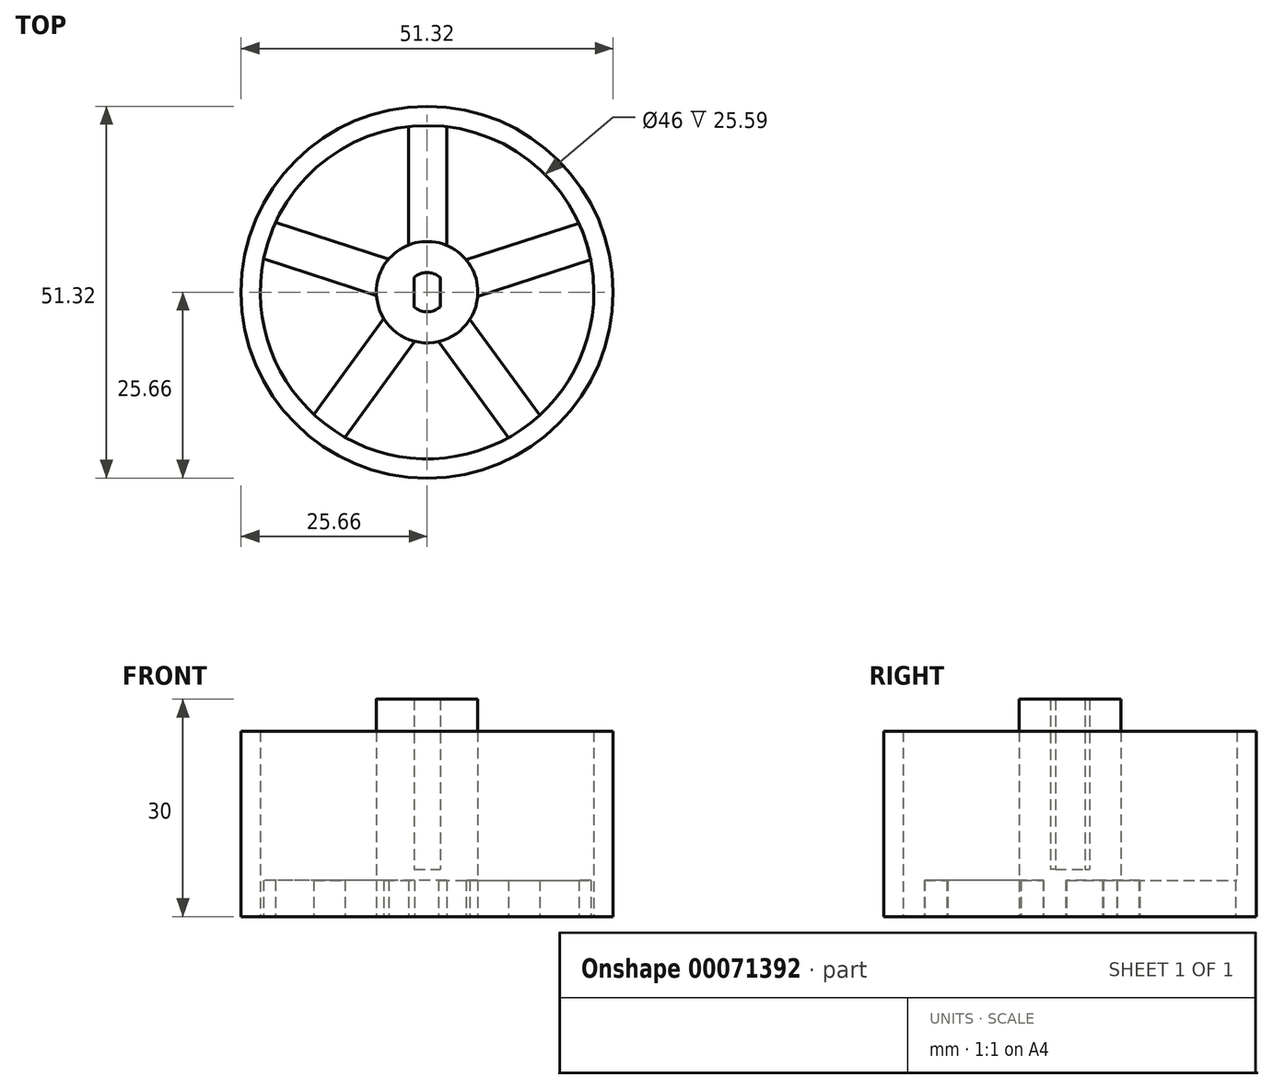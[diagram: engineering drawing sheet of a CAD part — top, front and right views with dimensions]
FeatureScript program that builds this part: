
annotation { "Feature Type Name" : "Feature", "Feature Type Description" : "" }
export const myFeature = defineFeature(function(context is Context, id is Id, definition is map)
    precondition{}
    {
        {
            var Q0;
            Q0=qCreatedBy(makeId("Top.planeOp"),FACE);
            var sketch = newSketch(context, id + "F0", { "sketchPlane" : qUnion([Q0])});
            skCircle(sketch, "E0", {"center": v(0, 0) * mm, "radius": 7 * mm});
            skCircle(sketch, "E1", {"center": v(0, 0) * mm, "radius": 23 * mm});
            skCircle(sketch, "E2", {"center": v(0, 0) * mm, "radius": 25.66 * mm});
            skLineSegment(sketch, "E3", {"start": v(-2.59, 6.5) * mm, "end": v(-2.59, 22.85) * mm});
            skLineSegment(sketch, "E4", {"start": v(2.71, 6.45) * mm, "end": v(2.71, 22.84) * mm});
            skLineSegment(sketch, "E5", {"start": v(-42.68, 0) * mm, "end": v(36.45, 0) * mm, "construction": true});
            skLineSegment(sketch, "E6", {"start": v(0, -31.73) * mm, "end": v(0, 31.16) * mm, "construction": true});
            skLineSegment(sketch, "E7.1.0", {"start": v(-6.99, -0.45) * mm, "end": v(-22.53, 4.6) * mm});
            skLineSegment(sketch, "E7.1.1", {"start": v(-5.3, 4.57) * mm, "end": v(-20.88, 9.64) * mm});
            skLineSegment(sketch, "E7.2.0", {"start": v(-1.73, -6.78) * mm, "end": v(-11.34, -20) * mm});
            skLineSegment(sketch, "E7.2.1", {"start": v(-5.99, -3.63) * mm, "end": v(-15.62, -16.88) * mm});
            skLineSegment(sketch, "E7.3.0", {"start": v(5.92, -3.74) * mm, "end": v(15.52, -16.97) * mm});
            skLineSegment(sketch, "E7.3.1", {"start": v(1.6, -6.82) * mm, "end": v(11.23, -20.07) * mm});
            skLineSegment(sketch, "E7.4.0", {"start": v(5.39, 4.47) * mm, "end": v(20.94, 9.52) * mm});
            skLineSegment(sketch, "E7.4.1", {"start": v(6.98, -0.59) * mm, "end": v(22.56, 4.48) * mm});
            skArc(sketch, "E8", {"start": v(-1.8, -2.03) * mm, "mid": v(0, -2.71) * mm, "end": v(1.8, -2.03) * mm});
            skLineSegment(sketch, "E9.left", {"start": v(1.8, -2.03) * mm, "end": v(1.8, 2.03) * mm});
            skLineSegment(sketch, "E9.right", {"start": v(-1.8, -2.03) * mm, "end": v(-1.8, 2.03) * mm});
            skArc(sketch, "E10.trimOffspring", {"start": v(1.8, 2.03) * mm, "mid": v(0, 2.72) * mm, "end": v(-1.8, 2.03) * mm});
            skSolve(sketch);
        }
        {
            var Q0;
            Q0=makeQuery(id+"F0.imprint","IMPRINT",FACE,{"disambiguationData":[TD([[makeQuery(id+"F0.imprint","IMPRINT",EDGE,{"derivedFrom":sQuery(id+"F0.wireOp",EDGE,"E9.bottom")}),-1.0]])]});
            var Q1;
            Q1=makeQuery(id+"F0.imprint","IMPRINT",FACE,{"disambiguationData":[TD([[makeQuery(id+"F0.imprint","IMPRINT",EDGE,{"derivedFrom":sQuery(id+"F0.wireOp",EDGE,"E8")}),1.0]])]});
            var Q2;
            Q2=makeQuery(id+"F0.imprint","IMPRINT",FACE,{"disambiguationData":[TD([[makeQuery(id+"F0.imprint","IMPRINT",EDGE,{"derivedFrom":sQuery(id+"F0.wireOp",EDGE,"E9.top")}),-1.0]])]});
            extrude(context, id + "F1", {"entities" : qUnion([Q0, Q1, Q2]), "depth" : 6.5 * mm});
        }
        {
            var Q0;
            Q0=makeQuery(id+"F0.imprint","IMPRINT",FACE,{"disambiguationData":[TD([[makeQuery(id+"F0.imprint","IMPRINT",EDGE,{"derivedFrom":sQuery(id+"F0.wireOp",EDGE,"E1")}),-1.0]])]});
            extrude(context, id + "F2", {"entities" : qUnion([Q0]), "depth" : 25.59 * mm});
        }
        {
            var Q0;
            {var subQ0=sQuery(id+"F0.wireOp",EDGE,"E3");Q0=makeQuery(id+"F0.imprint","IMPRINT",FACE,{"disambiguationData":[TD([[makeQuery(id+"F0.imprint","IMPRINT",EDGE,{"derivedFrom":subQ0}),-1.0]])]});}
            var Q1;
            {var subQ0=sQuery(id+"F0.wireOp",EDGE,"E7.1.0");Q1=makeQuery(id+"F0.imprint","IMPRINT",FACE,{"disambiguationData":[TD([[makeQuery(id+"F0.imprint","IMPRINT",EDGE,{"derivedFrom":subQ0}),-1.0]])]});}
            var Q2;
            {var subQ0=sQuery(id+"F0.wireOp",EDGE,"E7.2.0");Q2=makeQuery(id+"F0.imprint","IMPRINT",FACE,{"disambiguationData":[TD([[makeQuery(id+"F0.imprint","IMPRINT",EDGE,{"derivedFrom":subQ0}),-1.0]])]});}
            var Q3;
            {var subQ0=sQuery(id+"F0.wireOp",EDGE,"E7.3.0");Q3=makeQuery(id+"F0.imprint","IMPRINT",FACE,{"disambiguationData":[TD([[makeQuery(id+"F0.imprint","IMPRINT",EDGE,{"derivedFrom":subQ0}),-1.0]])]});}
            var Q4;
            {var subQ0=sQuery(id+"F0.wireOp",EDGE,"E7.4.0");Q4=makeQuery(id+"F0.imprint","IMPRINT",FACE,{"disambiguationData":[TD([[makeQuery(id+"F0.imprint","IMPRINT",EDGE,{"derivedFrom":subQ0}),-1.0]])]});}
            extrude(context, id + "F3", {"entities" : qUnion([Q0, Q1, Q2, Q3, Q4]), "operationType" : NewBodyOperationType.ADD, "depth" : 5 * mm});
        }
        {
            var Q0;
            {var subQ0=sQuery(id+"F0.wireOp",EDGE,"E0");var subQ6=makeQuery(id+"F0.imprint","INTERSECT",VERTEX,{"derivedFrom":[subQ0,sQuery(id+"F0.wireOp",EDGE,"E4")]});Q0=makeQuery(id+"F0.imprint","IMPRINT",FACE,{"disambiguationData":[TD([[makeQuery(id+"F0.imprint","IMPRINT",EDGE,{"disambiguationData":[TD([[subQ6,1.0]])],"derivedFrom":subQ0}),1.0]])]});}
            extrude(context, id + "F4", {"entities" : qUnion([Q0]), "operationType" : NewBodyOperationType.ADD, "depth" : 30 * mm});
        }
    });
